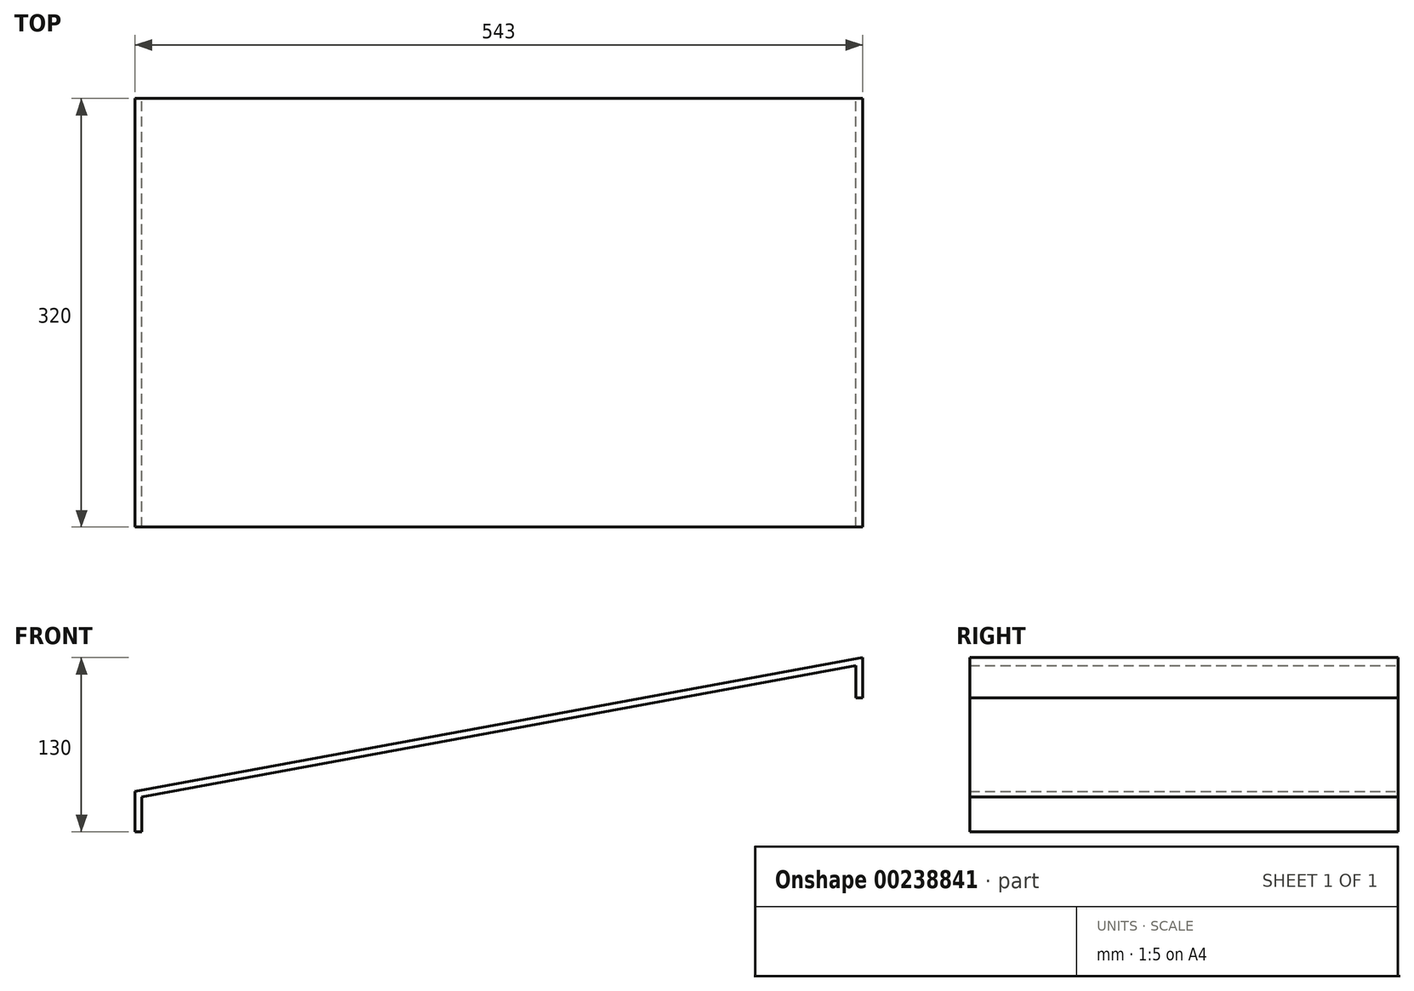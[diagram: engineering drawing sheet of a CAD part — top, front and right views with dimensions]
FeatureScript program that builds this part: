
annotation { "Feature Type Name" : "Feature", "Feature Type Description" : "" }
export const myFeature = defineFeature(function(context is Context, id is Id, definition is map)
    precondition{}
    {
        {
            var Q0;
            Q0=qCreatedBy(makeId("Front.planeOp"),FACE);
            var sketch = newSketch(context, id + "F0", { "sketchPlane" : qUnion([Q0])});
            skLineSegment(sketch, "E0", {"start": v(0, -30) * mm, "end": v(0, 0) * mm});
            skLineSegment(sketch, "E1", {"start": v(0, 0) * mm, "end": v(543, 100) * mm});
            skLineSegment(sketch, "E2", {"start": v(543, 100) * mm, "end": v(543, 70) * mm});
            skLineSegment(sketch, "E3", {"start": v(543, 70) * mm, "end": v(538, 70) * mm});
            skLineSegment(sketch, "E4", {"start": v(538, 70) * mm, "end": v(538, 94) * mm});
            skLineSegment(sketch, "E5", {"start": v(538, 94) * mm, "end": v(5, -4.16) * mm});
            skLineSegment(sketch, "E6", {"start": v(5, -4.16) * mm, "end": v(5, -30) * mm});
            skLineSegment(sketch, "E7", {"start": v(5, -30) * mm, "end": v(0, -30) * mm});
            skSolve(sketch);
        }
        {
            var Q0;
            Q0=makeQuery(id+"F0.imprint","IMPRINT",FACE,{"disambiguationData":[TD([[makeQuery(id+"F0.imprint","IMPRINT",EDGE,{"derivedFrom":sQuery(id+"F0.wireOp",EDGE,"E0")}),-1.0]])]});
            extrude(context, id + "F1", {"entities" : qUnion([Q0]), "depth" : 320 * mm});
        }
    });
